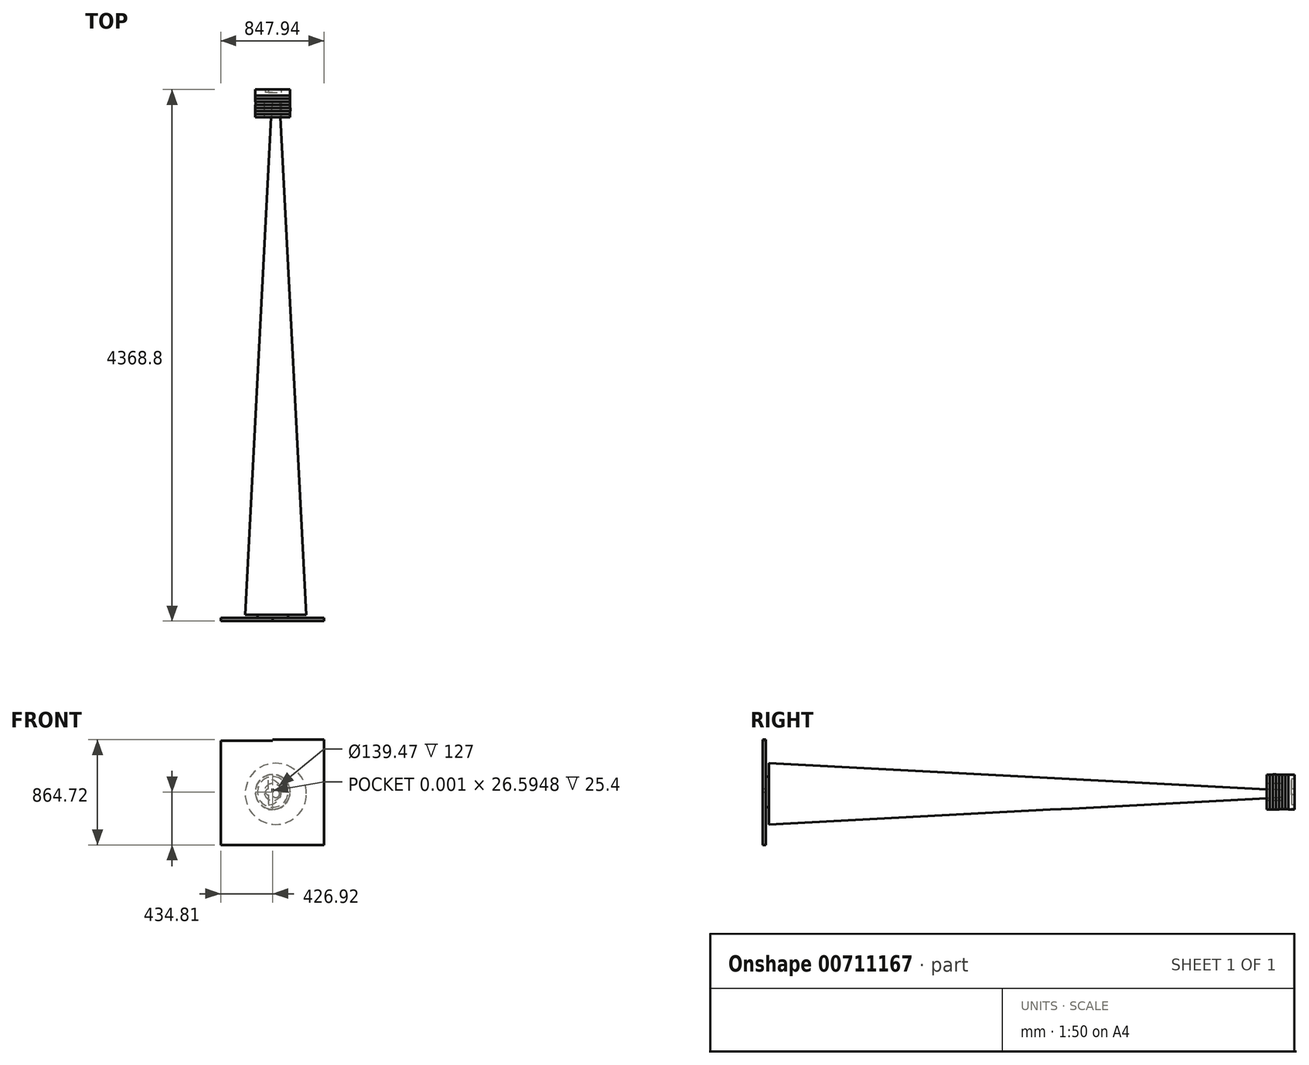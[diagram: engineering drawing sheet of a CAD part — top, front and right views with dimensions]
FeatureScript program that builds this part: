
annotation { "Feature Type Name" : "Feature", "Feature Type Description" : "" }
export const myFeature = defineFeature(function(context is Context, id is Id, definition is map)
    precondition{}
    {
        {
            var Q0;
            Q0=qCreatedBy(makeId("Front.planeOp"),FACE);
            var sketch = newSketch(context, id + "F0", { "sketchPlane" : qUnion([Q0])});
            skCircle(sketch, "E0", {"center": v(0, 0) * mm, "radius": 141.67 * mm});
            skSolve(sketch);
        }
        {
            var Q0;
            Q0 = qSketchRegion(id + "F0", true);
            extrude(context, id + "F1", {"entities" : qUnion([Q0]), "oppositeDirection" : true, "depth" : 25.4 * mm, "offsetDistance" : 25.4 * mm});
        }
        {
            var Q0;
            Q0=makeQuery(id+"F1.opExtrude","CAP_FACE",FACE,{"disambiguationData":[OSD([sQuery(id+"F0.wireOp",EDGE,"E0")])],"isStart":false});
            var sketch = newSketch(context, id + "F2", { "sketchPlane" : qUnion([Q0])});
            skCircle(sketch, "E1", {"center": v(0, 0) * mm, "radius": 142.1 * mm});
            skSolve(sketch);
        }
        {
            var Q0;
            Q0 = qSketchRegion(id + "F2", true);
            extrude(context, id + "F3", {"entities" : qUnion([Q0]), "operationType" : NewBodyOperationType.ADD, "depth" : 25.4 * mm, "offsetDistance" : 25.4 * mm});
        }
        {
            var Q0;
            Q0=makeQuery(id+"F3.opExtrude","CAP_FACE",FACE,{"disambiguationData":[OSD([sQuery(id+"F2.wireOp",EDGE,"E1")])],"isStart":false});
            var sketch = newSketch(context, id + "F4", { "sketchPlane" : qUnion([Q0])});
            skCircle(sketch, "E2", {"center": v(0, 0) * mm, "radius": 142.23 * mm});
            skSolve(sketch);
        }
        {
            var Q0;
            Q0 = qSketchRegion(id + "F4", true);
            extrude(context, id + "F5", {"entities" : qUnion([Q0]), "operationType" : NewBodyOperationType.ADD, "depth" : 25.4 * mm, "offsetDistance" : 25.4 * mm});
        }
        {
            var Q0;
            Q0=makeQuery(id+"F1.opExtrude","CAP_FACE",FACE,{"disambiguationData":[OSD([sQuery(id+"F0.wireOp",EDGE,"E0")])],"isStart":true});
            var sketch = newSketch(context, id + "F6", { "sketchPlane" : qUnion([Q0])});
            skCircle(sketch, "E3", {"center": v(0, 0) * mm, "radius": 143.44 * mm});
            skSolve(sketch);
        }
        {
            var Q0;
            Q0 = qSketchRegion(id + "F6", true);
            extrude(context, id + "F7", {"entities" : qUnion([Q0]), "operationType" : NewBodyOperationType.ADD, "depth" : 25.4 * mm, "offsetDistance" : 25.4 * mm});
        }
        {
            var Q0;
            Q0=makeQuery(id+"F5.opExtrude","CAP_FACE",FACE,{"disambiguationData":[OSD([sQuery(id+"F4.wireOp",EDGE,"E2")])],"isStart":false});
            var sketch = newSketch(context, id + "F8", { "sketchPlane" : qUnion([Q0])});
            skCircle(sketch, "E4", {"center": v(0, 0) * mm, "radius": 142.52 * mm});
            skSolve(sketch);
        }
        {
            var Q0;
            Q0 = qSketchRegion(id + "F8", true);
            extrude(context, id + "F9", {"entities" : qUnion([Q0]), "operationType" : NewBodyOperationType.ADD, "depth" : 25.4 * mm, "offsetDistance" : 25.4 * mm});
        }
        {
            var Q0;
            Q0=makeQuery(id+"F7.opExtrude","CAP_FACE",FACE,{"disambiguationData":[OSD([sQuery(id+"F6.wireOp",EDGE,"E3")])],"isStart":false});
            var sketch = newSketch(context, id + "F10", { "sketchPlane" : qUnion([Q0])});
            skCircle(sketch, "E5", {"center": v(0, 0) * mm, "radius": 143.86 * mm});
            skSolve(sketch);
        }
        {
            var Q0;
            Q0 = qSketchRegion(id + "F10", true);
            extrude(context, id + "F11", {"entities" : qUnion([Q0]), "operationType" : NewBodyOperationType.ADD, "depth" : 25.4 * mm, "offsetDistance" : 25.4 * mm});
        }
        {
            var Q0;
            Q0=makeQuery(id+"F11.opExtrude","CAP_FACE",FACE,{"disambiguationData":[OSD([sQuery(id+"F10.wireOp",EDGE,"E5")])],"isStart":false});
            var sketch = newSketch(context, id + "F12", { "sketchPlane" : qUnion([Q0])});
            skCircle(sketch, "E6", {"center": v(0, 0) * mm, "radius": 143 * mm});
            skSolve(sketch);
        }
        {
            var Q0;
            Q0 = qSketchRegion(id + "F12", true);
            extrude(context, id + "F13", {"entities" : qUnion([Q0]), "operationType" : NewBodyOperationType.ADD, "depth" : 25.4 * mm, "offsetDistance" : 25.4 * mm});
        }
        {
            var Q0;
            Q0=makeQuery(id+"F13.opExtrude","CAP_FACE",FACE,{"disambiguationData":[OSD([sQuery(id+"F12.wireOp",EDGE,"E6")])],"isStart":false});
            var sketch = newSketch(context, id + "F14", { "sketchPlane" : qUnion([Q0])});
            skCircle(sketch, "E7", {"center": v(0, 0) * mm, "radius": 143.15 * mm});
            skSolve(sketch);
        }
        {
            var Q0;
            Q0 = qSketchRegion(id + "F14", true);
            extrude(context, id + "F15", {"entities" : qUnion([Q0]), "operationType" : NewBodyOperationType.ADD, "depth" : 25.4 * mm, "offsetDistance" : 25.4 * mm});
        }
        {
            var Q0;
            Q0=makeQuery(id+"F15.opExtrude","CAP_FACE",FACE,{"disambiguationData":[OSD([sQuery(id+"F14.wireOp",EDGE,"E7")])],"isStart":false});
            var sketch = newSketch(context, id + "F16", { "sketchPlane" : qUnion([Q0])});
            skCircle(sketch, "E8", {"center": v(0, 0) * mm, "radius": 69.73 * mm});
            skSolve(sketch);
        }
        {
            var Q0;
            Q0 = qSketchRegion(id + "F16", true);
            extrude(context, id + "F17", {"entities" : qUnion([Q0]), "operationType" : NewBodyOperationType.REMOVE, "oppositeDirection" : true, "depth" : 127 * mm, "offsetDistance" : 25.4 * mm});
        }
        {
            var Q0;
            Q0=makeQuery(id+"F17.boolean.opBoolean","COPY",FACE,{"derivedFrom":makeQuery(id+"F17.opExtrude","CAP_FACE",FACE,{"disambiguationData":[OSD([sQuery(id+"F16.wireOp",EDGE,"E8")])],"isStart":false})});
            var sketch = newSketch(context, id + "F18", { "sketchPlane" : qUnion([Q0])});
            skCircle(sketch, "E9", {"center": v(25.34, -14.92) * mm, "radius": 30.68 * mm});
            skSolve(sketch);
        }
        {
            var Q0;
            Q0 = qSketchRegion(id + "F18", true);
            extrude(context, id + "F19", {"entities" : qUnion([Q0]), "operationType" : NewBodyOperationType.ADD, "depth" : 4216.4 * mm, "offsetDistance" : 25.4 * mm, "hasDraft" : true, "draftAngle" : 3 * degree});
        }
        {
            var Q0;
            Q0=makeQuery(id+"F19.opExtrude","CAP_FACE",FACE,{"disambiguationData":[OSD([sQuery(id+"F18.wireOp",EDGE,"E9")])],"isStart":false});
            var sketch = newSketch(context, id + "F20", { "sketchPlane" : qUnion([Q0])});
            skCircle(sketch, "E10", {"center": v(0, 0) * mm, "radius": 125.38 * mm});
            skSolve(sketch);
        }
        {
            var Q0;
            Q0 = qSketchRegion(id + "F20", true);
            extrude(context, id + "F21", {"entities" : qUnion([Q0]), "operationType" : NewBodyOperationType.ADD, "depth" : 25.4 * mm, "offsetDistance" : 25.4 * mm});
        }
        {
            var Q0;
            Q0=makeQuery(id+"F21.opExtrude","CAP_FACE",FACE,{"disambiguationData":[OSD([sQuery(id+"F20.wireOp",EDGE,"E10")])],"isStart":false});
            var sketch = newSketch(context, id + "F22", { "sketchPlane" : qUnion([Q0])});
            skLineSegment(sketch, "E11.bottom", {"start": v(0, 0) * mm, "end": v(0, 0) * mm});
            skLineSegment(sketch, "E11.top", {"start": v(0, 429.91) * mm, "end": v(0, 429.91) * mm});
            skLineSegment(sketch, "E11.left", {"start": v(0, 0) * mm, "end": v(0, 429.91) * mm});
            skLineSegment(sketch, "E11.right", {"start": v(0, 0) * mm, "end": v(0, 429.91) * mm});
            skLineSegment(sketch, "E12.bottom", {"start": v(0, 429.91) * mm, "end": v(421.02, 429.91) * mm});
            skLineSegment(sketch, "E12.top", {"start": v(0, -434.8) * mm, "end": v(421.02, -434.8) * mm});
            skLineSegment(sketch, "E12.left", {"start": v(0, 429.91) * mm, "end": v(0, -434.8) * mm});
            skLineSegment(sketch, "E12.right", {"start": v(421.02, 429.91) * mm, "end": v(421.02, -434.8) * mm});
            skLineSegment(sketch, "E13.bottom", {"start": v(0, 26.6) * mm, "end": v(-426.92, 26.6) * mm});
            skLineSegment(sketch, "E13.top", {"start": v(0, 422.87) * mm, "end": v(-426.92, 422.87) * mm});
            skLineSegment(sketch, "E13.left", {"start": v(0, 26.6) * mm, "end": v(0, 422.87) * mm});
            skLineSegment(sketch, "E13.right", {"start": v(-426.92, 26.6) * mm, "end": v(-426.92, 422.87) * mm});
            skLineSegment(sketch, "E14.bottom", {"start": v(-426.92, 26.6) * mm, "end": v(0, 26.6) * mm});
            skLineSegment(sketch, "E14.top", {"start": v(-426.92, -434.8) * mm, "end": v(0, -434.8) * mm});
            skLineSegment(sketch, "E14.left", {"start": v(-426.92, 26.6) * mm, "end": v(-426.92, -434.8) * mm});
            skLineSegment(sketch, "E14.right", {"start": v(0, 26.6) * mm, "end": v(0, -434.8) * mm});
            skLineSegment(sketch, "E15.bottom", {"start": v(0, 26.6) * mm, "end": v(421.02, 26.6) * mm});
            skLineSegment(sketch, "E15.top", {"start": v(0, 26.6) * mm, "end": v(421.02, 26.6) * mm});
            skLineSegment(sketch, "E15.left", {"start": v(0, 26.6) * mm, "end": v(0, 26.6) * mm});
            skLineSegment(sketch, "E15.right", {"start": v(421.02, 26.6) * mm, "end": v(421.02, 26.6) * mm});
            skSolve(sketch);
        }
        {
            var Q0;
            Q0 = qSketchRegion(id + "F22", true);
            extrude(context, id + "F23", {"entities" : qUnion([Q0]), "operationType" : NewBodyOperationType.ADD, "depth" : 25.4 * mm, "offsetDistance" : 25.4 * mm});
        }
        {
            var Q0;
            Q0=makeQuery(id+"F9.opExtrude","CAP_FACE",FACE,{"disambiguationData":[OSD([sQuery(id+"F8.wireOp",EDGE,"E4")])],"isStart":false});
            var sketch = newSketch(context, id + "F24", { "sketchPlane" : qUnion([Q0])});
            skLineSegment(sketch, "E16.bottom", {"start": v(0, 0) * mm, "end": v(36.27, 0) * mm});
            skLineSegment(sketch, "E16.top", {"start": v(0, 137.83) * mm, "end": v(36.27, 137.83) * mm});
            skLineSegment(sketch, "E16.left", {"start": v(0, 0) * mm, "end": v(0, 137.83) * mm});
            skLineSegment(sketch, "E16.right", {"start": v(36.27, 0) * mm, "end": v(36.27, 137.83) * mm});
            skLineSegment(sketch, "E17.bottom", {"start": v(36.27, 0) * mm, "end": v(0, 0) * mm});
            skLineSegment(sketch, "E17.top", {"start": v(36.27, -142.52) * mm, "end": v(0, -142.52) * mm});
            skLineSegment(sketch, "E17.left", {"start": v(36.27, 0) * mm, "end": v(36.27, -142.52) * mm});
            skLineSegment(sketch, "E17.right", {"start": v(0, 0) * mm, "end": v(0, -142.52) * mm});
            skCircle(sketch, "E18", {"center": v(36.27, 0) * mm, "radius": 106.25 * mm});
            skCircle(sketch, "E19", {"center": v(36.27, 0) * mm, "radius": 23.62 * mm});
            skCircle(sketch, "E20", {"center": v(0, 0) * mm, "radius": 12.65 * mm});
            skCircle(sketch, "E21", {"center": v(0, 0) * mm, "radius": 142.52 * mm});
            skSolve(sketch);
        }
        {
            var Q0;
            Q0 = qSketchRegion(id + "F24", true);
            extrude(context, id + "F25", {"entities" : qUnion([Q0]), "operationType" : NewBodyOperationType.ADD, "depth" : 25.4 * mm, "offsetDistance" : 25.4 * mm});
        }
    });
